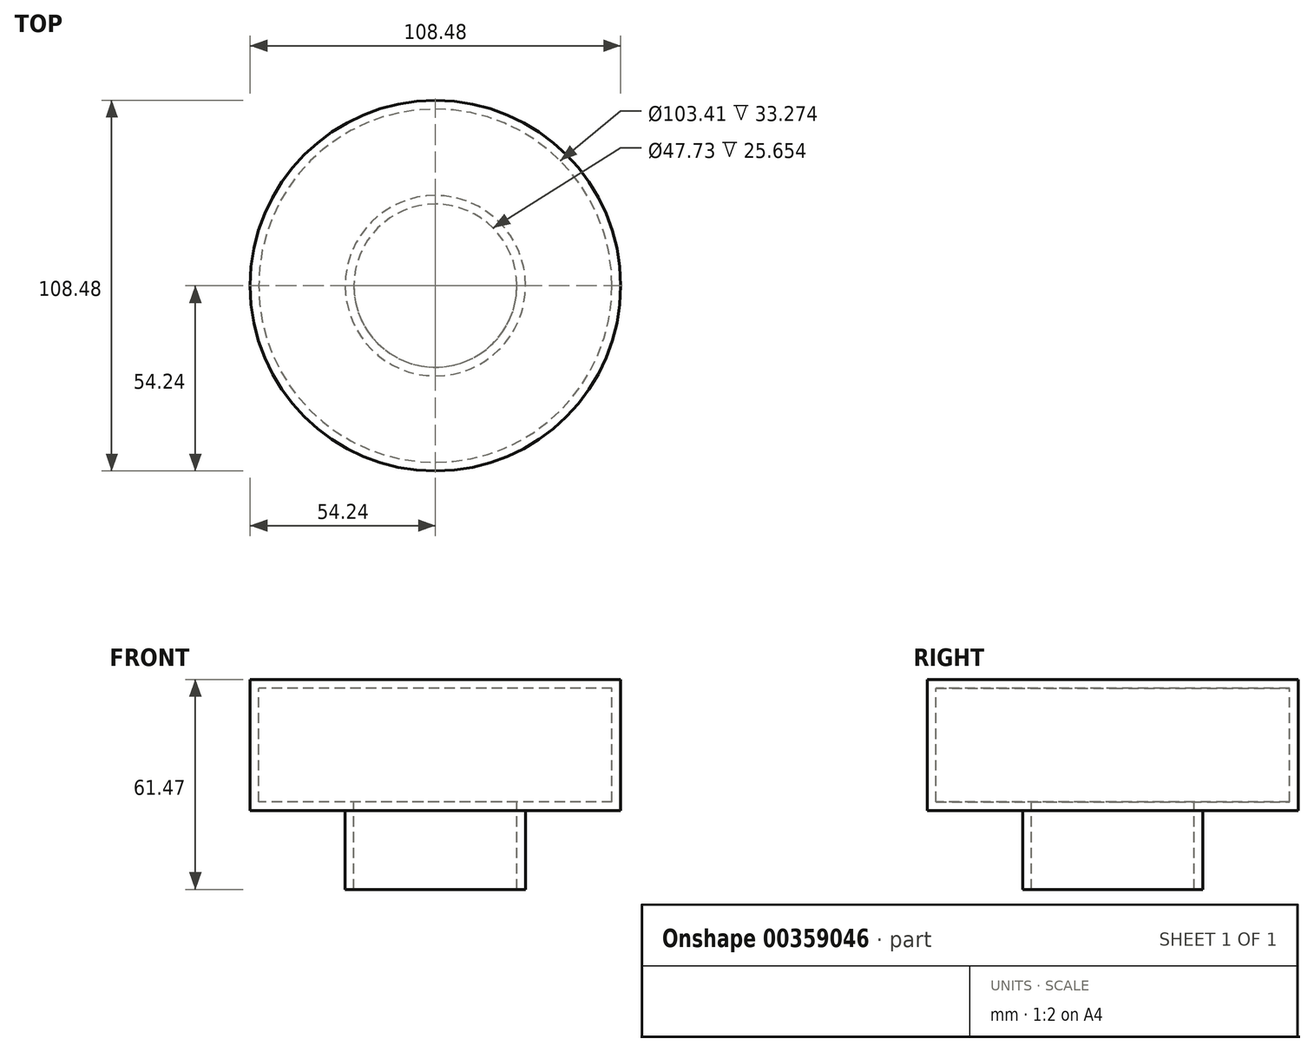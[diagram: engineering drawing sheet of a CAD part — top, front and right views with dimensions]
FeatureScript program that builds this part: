
annotation { "Feature Type Name" : "Feature", "Feature Type Description" : "" }
export const myFeature = defineFeature(function(context is Context, id is Id, definition is map)
    precondition{}
    {
        {
            var Q0;
            Q0=qCreatedBy(makeId("Top.planeOp"),FACE);
            var sketch = newSketch(context, id + "F0", { "sketchPlane" : qUnion([Q0])});
            skCircle(sketch, "E0", {"center": v(0, 0) * mm, "radius": 54.24 * mm});
            skSolve(sketch);
        }
        {
            var Q0;
            Q0=makeQuery(id+"F0.imprint","IMPRINT",FACE,{"disambiguationData":[TD([[makeQuery(id+"F0.imprint","IMPRINT",EDGE,{"derivedFrom":sQuery(id+"F0.wireOp",EDGE,"E0")}),1.0]])]});
            extrude(context, id + "F1", {"entities" : qUnion([Q0]), "oppositeDirection" : true, "depth" : 38.35 * mm});
        }
        {
            var Q0;
            Q0=makeQuery(id+"F1.opExtrude","CAP_FACE",FACE,{"disambiguationData":[OSD([sQuery(id+"F0.wireOp",EDGE,"E0")])],"isStart":false});
            var sketch = newSketch(context, id + "F2", { "sketchPlane" : qUnion([Q0])});
            skCircle(sketch, "E1", {"center": v(0, 0) * mm, "radius": 26.4 * mm});
            skSolve(sketch);
        }
        {
            var Q0;
            Q0=makeQuery(id+"F2.imprint","IMPRINT",FACE,{"disambiguationData":[TD([[makeQuery(id+"F2.imprint","IMPRINT",EDGE,{"derivedFrom":sQuery(id+"F2.wireOp",EDGE,"E1")}),1.0]])]});
            extrude(context, id + "F3", {"entities" : qUnion([Q0]), "operationType" : NewBodyOperationType.ADD, "depth" : 23.1 * mm});
        }
        {
            var Q0;
            Q0=makeQuery(id+"F3.opExtrude","CAP_FACE",FACE,{"disambiguationData":[OSD([sQuery(id+"F2.wireOp",EDGE,"E1")])],"isStart":false});
            shell(context, id + "F4", {"entities" : qUnion([Q0]), "thickness" : 2.54 * mm});
        }
    });
